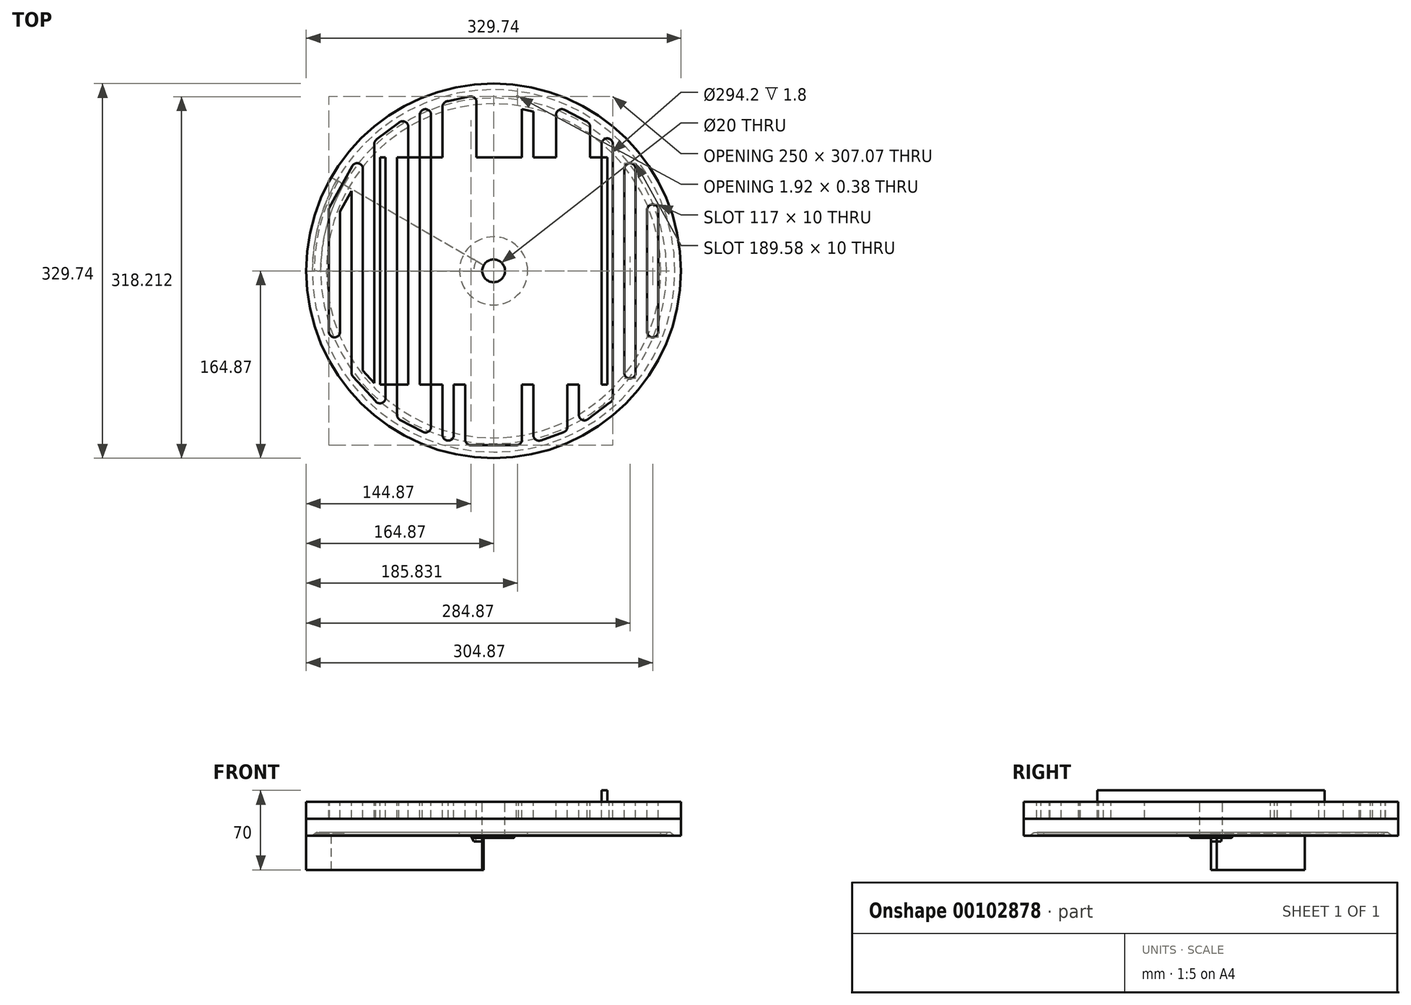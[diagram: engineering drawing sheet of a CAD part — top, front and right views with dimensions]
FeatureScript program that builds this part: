
annotation { "Feature Type Name" : "Feature", "Feature Type Description" : "" }
export const myFeature = defineFeature(function(context is Context, id is Id, definition is map)
    precondition{}
    {
        {
            var Q0;
            Q0=qCreatedBy(makeId("Front.planeOp"),FACE);
            var sketch = newSketch(context, id + "F0", { "sketchPlane" : qUnion([Q0])});
            skLineSegment(sketch, "E0", {"start": v(-152.8, 6.54) * mm, "end": v(-147.1, 6.54) * mm});
            skLineSegment(sketch, "E1", {"start": v(0, 31.7) * mm, "end": v(0, -32.2) * mm});
            skLineSegment(sketch, "E2", {"start": v(-19.86, 6.26) * mm, "end": v(-17.5, 1.54) * mm});
            skLineSegment(sketch, "E3.0", {"start": v(-155.24, 8.34) * mm, "end": v(-153.54, 8.34) * mm});
            skLineSegment(sketch, "E4", {"start": v(-155.48, 8.26) * mm, "end": v(-157.85, 6.54) * mm});
            skPoint(sketch, "E5.visualSharp", {"position": v(-153.6, 6.54) * mm});
            skArc(sketch, "E5.filletArc", {"start": v(-153.1, 6.79) * mm, "mid": v(-153, 6.6) * mm, "end": v(-152.8, 6.54) * mm});
            skLineSegment(sketch, "E6", {"start": v(-153.34, 8.17) * mm, "end": v(-153.1, 6.79) * mm});
            skPoint(sketch, "E7.visualSharp", {"position": v(-153.37, 8.34) * mm});
            skArc(sketch, "E7.filletArc", {"start": v(-153.34, 8.17) * mm, "mid": v(-153.41, 8.3) * mm, "end": v(-153.54, 8.34) * mm});
            skPoint(sketch, "E8.visualSharp", {"position": v(-155.37, 8.34) * mm});
            skArc(sketch, "E8.filletArc", {"start": v(-155.24, 8.34) * mm, "mid": v(-155.37, 8.32) * mm, "end": v(-155.48, 8.26) * mm});
            skPoint(sketch, "E9.visualSharp", {"position": v(-20, 6.54) * mm});
            skArc(sketch, "E9.filletArc", {"start": v(-19.86, 6.26) * mm, "mid": v(-20.05, 6.46) * mm, "end": v(-20.3, 6.54) * mm});
            skLineSegment(sketch, "E10.0", {"start": v(-10, -3.46) * mm, "end": v(-10, -23.46) * mm});
            skPoint(sketch, "E11.endSnap0", {"position": v(-155.37, 8.32) * mm});
            skLineSegment(sketch, "E12.0", {"start": v(-164.87, 1.45) * mm, "end": v(-164.87, -23.46) * mm});
            skLineSegment(sketch, "E13.0", {"start": v(-164.87, -23.46) * mm, "end": v(-10, -23.46) * mm});
            skLineSegment(sketch, "E14.0", {"start": v(-147.1, 9.34) * mm, "end": v(-147.1, 7.54) * mm});
            skLineSegment(sketch, "E15", {"start": v(-154.4, 8.34) * mm, "end": v(-153.37, 8.34) * mm});
            skLineSegment(sketch, "E16", {"start": v(-10, -7.75) * mm, "end": v(-10, 8.34) * mm});
            skPoint(sketch, "E17.orphan", {"position": v(0, 8.34) * mm});
            skLineSegment(sketch, "E18", {"start": v(-164.87, 1.45) * mm, "end": v(-164.87, 36.54) * mm});
            skLineSegment(sketch, "E19", {"start": v(-164.87, 36.54) * mm, "end": v(-10, 36.54) * mm});
            skLineSegment(sketch, "E20", {"start": v(-10, 36.54) * mm, "end": v(-10, 8.34) * mm});
            skLineSegment(sketch, "E21", {"start": v(-30, 9.34) * mm, "end": v(-30, 7.54) * mm});
            skPoint(sketch, "E22.start.orphan", {"position": v(-15, -3.46) * mm});
            skLineSegment(sketch, "E23.trimOffspring", {"start": v(-30, 6.54) * mm, "end": v(-20.3, 6.54) * mm});
            skLineSegment(sketch, "E24", {"start": v(-17.5, 1.54) * mm, "end": v(-10, 1.54) * mm});
            skLineSegment(sketch, "E25", {"start": v(-164.87, 6.54) * mm, "end": v(-30, 6.54) * mm});
            skLineSegment(sketch, "E26.0", {"start": v(-17.25, 4.52) * mm, "end": v(-9.64, 4.52) * mm});
            skLineSegment(sketch, "E27.0", {"start": v(-152.22, 7.54) * mm, "end": v(-147.1, 7.54) * mm});
            skLineSegment(sketch, "E28.0", {"start": v(-156.06, 9.07) * mm, "end": v(-159.56, 6.54) * mm});
            skArc(sketch, "E29.0", {"start": v(-155.24, 9.34) * mm, "mid": v(-155.67, 9.27) * mm, "end": v(-156.06, 9.07) * mm});
            skLineSegment(sketch, "E30.0", {"start": v(-155.24, 9.34) * mm, "end": v(-153.04, 9.34) * mm});
            skLineSegment(sketch, "E31.0", {"start": v(-152.44, 8.84) * mm, "end": v(-152.22, 7.54) * mm});
            skLineSegment(sketch, "E32.0", {"start": v(-147.1, 9.34) * mm, "end": v(-30, 9.34) * mm});
            skLineSegment(sketch, "E33.0", {"start": v(-30, 7.54) * mm, "end": v(-20.3, 7.54) * mm});
            skLineSegment(sketch, "E34.0", {"start": v(-18.97, 6.7) * mm, "end": v(-18.15, 5.07) * mm});
            skArc(sketch, "E35.0", {"start": v(-18.97, 6.7) * mm, "mid": v(-19.52, 7.31) * mm, "end": v(-20.3, 7.54) * mm});
            skPoint(sketch, "E36.trimOffspring.end.orphan", {"position": v(-30, 8.34) * mm});
            skPoint(sketch, "E37.visualSharp", {"position": v(-152.53, 9.34) * mm});
            skArc(sketch, "E37.filletArc", {"start": v(-152.44, 8.84) * mm, "mid": v(-152.65, 9.2) * mm, "end": v(-153.04, 9.34) * mm});
            skPoint(sketch, "E38.visualSharp", {"position": v(-17.87, 4.52) * mm});
            skArc(sketch, "E38.filletArc", {"start": v(-18.15, 5.07) * mm, "mid": v(-17.78, 4.67) * mm, "end": v(-17.25, 4.52) * mm});
            skLineSegment(sketch, "E39", {"start": v(-147.1, 7.54) * mm, "end": v(-30, 7.54) * mm});
            skSolve(sketch);
        }
        {
            var Q0;
            {var subQ10=sQuery(id+"F0.wireOp",EDGE,"E9.filletArc");Q0=makeQuery(id+"F0.imprint","IMPRINT",FACE,{"disambiguationData":[TD([[makeQuery(id+"F0.imprint","IMPRINT",EDGE,{"derivedFrom":subQ10}),1.0]])]});}
            var Q1;
            {var subQ2=sQuery(id+"F0.wireOp",EDGE,"E3.0");Q1=makeQuery(id+"F0.imprint","IMPRINT",FACE,{"disambiguationData":[TD([[makeQuery(id+"F0.imprint","IMPRINT",EDGE,{"derivedFrom":subQ2}),-1.0]])]});}
            var Q2;
            Q2=sQuery(id+"F0.wireOp",EDGE,"E1");
            revolve(context, id + "F1", {"entities" : qUnion([Q0, Q1]), "axis" : qUnion([Q2]), "revolveType" : RevolveType.ONE_DIRECTION, "angle" : 30 * degree});
        }
        {
            var Q0;
            {var subQ2=sQuery(id+"F0.wireOp",EDGE,"E9.filletArc");Q0=makeQuery(id+"F0.imprint","IMPRINT",FACE,{"disambiguationData":[TD([[makeQuery(id+"F0.imprint","IMPRINT",EDGE,{"derivedFrom":subQ2}),-1.0]])]});}
            var Q1;
            {var subQ1=sQuery(id+"F0.wireOp",EDGE,"E3.0");Q1=makeQuery(id+"F0.imprint","IMPRINT",FACE,{"disambiguationData":[TD([[makeQuery(id+"F0.imprint","IMPRINT",EDGE,{"derivedFrom":subQ1}),1.0]])]});}
            var Q2;
            Q2=sQuery(id+"F0.wireOp",EDGE,"E1");
            revolve(context, id + "F2", {"entities" : qUnion([Q0, Q1]), "axis" : qUnion([Q2]), "revolveType" : RevolveType.ONE_DIRECTION, "angle" : 30 * degree});
        }
        {
            var Q0;
            Q0=makeQuery(id+"F2.opRevolve","SWEPT_BODY",BODY,{"disambiguationData":[OSD([sQuery(id+"F0.wireOp",EDGE,"E2"),sQuery(id+"F0.wireOp",EDGE,"E3.0"),sQuery(id+"F0.wireOp",EDGE,"E4"),sQuery(id+"F0.wireOp",EDGE,"E5.filletArc"),sQuery(id+"F0.wireOp",EDGE,"E6"),sQuery(id+"F0.wireOp",EDGE,"E7.filletArc"),sQuery(id+"F0.wireOp",EDGE,"E8.filletArc"),sQuery(id+"F0.wireOp",EDGE,"E9.filletArc"),sQuery(id+"F0.wireOp",EDGE,"E14.0"),sQuery(id+"F0.wireOp",EDGE,"E15"),sQuery(id+"F0.wireOp",EDGE,"E16"),sQuery(id+"F0.wireOp",EDGE,"E18"),sQuery(id+"F0.wireOp",EDGE,"E19"),sQuery(id+"F0.wireOp",EDGE,"E20"),sQuery(id+"F0.wireOp",EDGE,"E36.trimOffspring"),sQuery(id+"F0.wireOp",EDGE,"E21"),sQuery(id+"F0.wireOp",EDGE,"E23.trimOffspring"),sQuery(id+"F0.wireOp",EDGE,"E25"),sQuery(id+"F0.wireOp",EDGE,"E26.0")])]});
            transform(context, id + "F3", {"entities" : qUnion([Q0]), "transformType" : TransformType.TRANSLATION_3D, "dx" : 0 * mm, "dy" : 0 * mm, "dz" : 0 * mm, "makeCopy" : false});
        }
        {
            var Q0;
            Q0=makeQuery(id+"F0.imprint","IMPRINT",FACE,{"disambiguationData":[TD([[makeQuery(id+"F0.imprint","IMPRINT",EDGE,{"derivedFrom":sQuery(id+"F0.wireOp",EDGE,"E14.0")}),-1.0]])]});
            var Q1;
            Q1=sQuery(id+"F0.wireOp",EDGE,"E1");
            revolve(context, id + "F4", {"entities" : qUnion([Q0]), "axis" : qUnion([Q1]), "revolveType" : RevolveType.FULL});
        }
        {
            var Q0;
            Q0=makeQuery(id+"F4.opRevolve","SWEPT_BODY",BODY,{"disambiguationData":[OSD([sQuery(id+"F0.wireOp",EDGE,"E14.0"),sQuery(id+"F0.wireOp",EDGE,"E16"),sQuery(id+"F0.wireOp",EDGE,"E18"),sQuery(id+"F0.wireOp",EDGE,"E19"),sQuery(id+"F0.wireOp",EDGE,"E20"),sQuery(id+"F0.wireOp",EDGE,"E21"),sQuery(id+"F0.wireOp",EDGE,"E25"),sQuery(id+"F0.wireOp",EDGE,"E26.0"),sQuery(id+"F0.wireOp",EDGE,"E27.0"),sQuery(id+"F0.wireOp",EDGE,"E28.0"),sQuery(id+"F0.wireOp",EDGE,"E29.0"),sQuery(id+"F0.wireOp",EDGE,"E30.0"),sQuery(id+"F0.wireOp",EDGE,"E31.0"),sQuery(id+"F0.wireOp",EDGE,"E32.0"),sQuery(id+"F0.wireOp",EDGE,"E33.0"),sQuery(id+"F0.wireOp",EDGE,"E34.0"),sQuery(id+"F0.wireOp",EDGE,"E35.0"),sQuery(id+"F0.wireOp",EDGE,"E37.filletArc"),sQuery(id+"F0.wireOp",EDGE,"E38.filletArc")])]});
            transform(context, id + "F5", {"entities" : qUnion([Q0]), "transformType" : TransformType.TRANSLATION_3D, "dx" : 0 * mm, "dy" : 0 * mm, "dz" : 0 * mm, "makeCopy" : false});
        }
        {
            var Q0;
            Q0=makeQuery(id+"F4.opRevolve","SWEPT_FACE",FACE,{"disambiguationData":[OSD([sQuery(id+"F0.wireOp",EDGE,"E19")])]});
            var sketch = newSketch(context, id + "F6", { "sketchPlane" : qUnion([Q0])});
            skLineSegment(sketch, "E40.right", {"start": v(100, 100) * mm, "end": v(100, -100) * mm});
            skPoint(sketch, "E40.middle", {"position": v(0, 0) * mm});
            skLineSegment(sketch, "E41.4.0.0", {"start": v(100, 111.64) * mm, "end": v(100, -111.64) * mm});
            skLineSegment(sketch, "E41.5.0.0", {"start": v(120, 89.8) * mm, "end": v(120, -89.8) * mm});
            skLineSegment(sketch, "E41.6.0.0", {"start": v(140, 53.5) * mm, "end": v(140, -53.5) * mm});
            skLineSegment(sketch, "E41.direction1", {"start": v(20, -149.87) * mm, "end": v(40, -149.87) * mm, "construction": true});
            skLineSegment(sketch, "E42.direction1", {"start": v(-20, -149.87) * mm, "end": v(-40, -149.87) * mm, "construction": true});
            skArc(sketch, "E43.0.startCap", {"start": v(-124.38, 92.2) * mm, "mid": v(-118.75, 94.63) * mm, "end": v(-115, 89.8) * mm});
            skArc(sketch, "E43.0.endCap", {"start": v(-123.69, -93.17) * mm, "mid": v(-124.66, -91.6) * mm, "end": v(-125, -89.8) * mm});
            skLineSegment(sketch, "E43.0.left", {"start": v(-115, 89.8) * mm, "end": v(-115, -87.85) * mm});
            skLineSegment(sketch, "E43.0.right", {"start": v(-125, 70.36) * mm, "end": v(-125, -89.8) * mm});
            skArc(sketch, "E43.1.startCap", {"start": v(-145, 53.5) * mm, "mid": v(-144.83, 54.79) * mm, "end": v(-144.34, 55.99) * mm});
            skArc(sketch, "E43.1.endCap", {"start": v(-135, -53.5) * mm, "mid": v(-140, -58.5) * mm, "end": v(-145, -53.5) * mm});
            skLineSegment(sketch, "E43.1.left", {"start": v(-135, 52.21) * mm, "end": v(-135, -53.5) * mm});
            skLineSegment(sketch, "E43.1.right", {"start": v(-145, 53.5) * mm, "end": v(-145, -53.5) * mm});
            skArc(sketch, "E43.2.startCap", {"start": v(-105, 111.64) * mm, "mid": v(-104.48, 113.87) * mm, "end": v(-103.01, 115.63) * mm});
            skArc(sketch, "E43.2.endCap", {"start": v(-95, -111.64) * mm, "mid": v(-98.28, -116.33) * mm, "end": v(-103.82, -114.86) * mm});
            skLineSegment(sketch, "E43.2.left", {"start": v(-95, 109.14) * mm, "end": v(-95, -111.64) * mm});
            skLineSegment(sketch, "E43.2.right", {"start": v(-105, 111.64) * mm, "end": v(-105, -98.77) * mm});
            skArc(sketch, "E43.3.startCap", {"start": v(-83.28, 130.51) * mm, "mid": v(-77.93, 131.29) * mm, "end": v(-75, 126.74) * mm});
            skArc(sketch, "E43.3.endCap", {"start": v(-82.34, -131.16) * mm, "mid": v(-84.28, -129.32) * mm, "end": v(-85, -126.74) * mm});
            skLineSegment(sketch, "E43.3.left", {"start": v(-75, 126.74) * mm, "end": v(-75, -123.73) * mm});
            skLineSegment(sketch, "E43.3.right", {"start": v(-85, 116.69) * mm, "end": v(-85, -126.74) * mm});
            skArc(sketch, "E43.4.startCap", {"start": v(-65, 137.34) * mm, "mid": v(-60, 142.34) * mm, "end": v(-55, 137.34) * mm});
            skArc(sketch, "E43.4.endCap", {"start": v(-55, -137.34) * mm, "mid": v(-57.64, -141.75) * mm, "end": v(-62.77, -141.5) * mm});
            skLineSegment(sketch, "E43.4.left", {"start": v(-55, 137.34) * mm, "end": v(-55, -137.34) * mm});
            skLineSegment(sketch, "E43.4.right", {"start": v(-65, 137.34) * mm, "end": v(-65, -129.01) * mm});
            skArc(sketch, "E43.5.startCap", {"start": v(-45, 144.44) * mm, "mid": v(-43.54, 147.97) * mm, "end": v(-40, 149.44) * mm});
            skArc(sketch, "E43.5.endCap", {"start": v(-35, -144.44) * mm, "mid": v(-40, -149.44) * mm, "end": v(-45, -144.44) * mm});
            skLineSegment(sketch, "E43.5.left", {"start": v(-35, 140.27) * mm, "end": v(-35, -144.44) * mm});
            skLineSegment(sketch, "E43.5.right", {"start": v(-45, 144.44) * mm, "end": v(-45, -144.44) * mm});
            skArc(sketch, "E43.6.startCap", {"start": v(-21.03, 153.43) * mm, "mid": v(-16.85, 152.42) * mm, "end": v(-15, 148.53) * mm});
            skArc(sketch, "E43.6.endCap", {"start": v(-20, -153.53) * mm, "mid": v(-23.54, -152.07) * mm, "end": v(-25, -148.53) * mm});
            skLineSegment(sketch, "E43.6.left", {"start": v(-15, 148.53) * mm, "end": v(-15, -143.53) * mm});
            skLineSegment(sketch, "E43.6.right", {"start": v(-25, 142.37) * mm, "end": v(-25, -148.53) * mm});
            skArc(sketch, "E43.8.startCap", {"start": v(15, 148.53) * mm, "mid": v(17.23, 152.7) * mm, "end": v(21.92, 153.15) * mm});
            skArc(sketch, "E43.8.endCap", {"start": v(25, -148.53) * mm, "mid": v(23.54, -152.07) * mm, "end": v(20, -153.53) * mm});
            skLineSegment(sketch, "E43.8.left", {"start": v(25, 142.34) * mm, "end": v(25, -148.53) * mm});
            skLineSegment(sketch, "E43.8.right", {"start": v(15, 148.53) * mm, "end": v(15, -143.53) * mm});
            skArc(sketch, "E43.9.startCap", {"start": v(40, 149.44) * mm, "mid": v(43.54, 147.97) * mm, "end": v(45, 144.44) * mm});
            skLineSegment(sketch, "E43.9.left", {"start": v(45, 144.44) * mm, "end": v(45, -137.44) * mm});
            skLineSegment(sketch, "E43.9.right", {"start": v(35, 140.34) * mm, "end": v(35, -144.56) * mm});
            skArc(sketch, "E43.10.startCap", {"start": v(55, 137.34) * mm, "mid": v(60, 142.34) * mm, "end": v(65, 137.34) * mm});
            skArc(sketch, "E43.10.endCap", {"start": v(65, -137.34) * mm, "mid": v(64.1, -140.21) * mm, "end": v(61.7, -142.04) * mm});
            skLineSegment(sketch, "E43.10.left", {"start": v(65, 137.34) * mm, "end": v(65, -137.34) * mm});
            skLineSegment(sketch, "E43.10.right", {"start": v(55, 137.34) * mm, "end": v(55, -133.83) * mm});
            skArc(sketch, "E43.11.startCap", {"start": v(75, 126.74) * mm, "mid": v(80, 131.74) * mm, "end": v(85, 126.74) * mm});
            skArc(sketch, "E43.11.endCap", {"start": v(83.04, -130.7) * mm, "mid": v(77.79, -131.22) * mm, "end": v(75, -126.74) * mm});
            skLineSegment(sketch, "E43.11.left", {"start": v(85, 126.74) * mm, "end": v(85, -116.6) * mm});
            skLineSegment(sketch, "E43.11.right", {"start": v(75, 126.74) * mm, "end": v(75, -126.74) * mm});
            skArc(sketch, "E43.12.startCap", {"start": v(95, 111.64) * mm, "mid": v(100, 116.64) * mm, "end": v(105, 111.64) * mm});
            skArc(sketch, "E43.12.endCap", {"start": v(105, -111.64) * mm, "mid": v(104.13, -114.46) * mm, "end": v(101.81, -116.3) * mm});
            skLineSegment(sketch, "E43.12.left", {"start": v(105, 111.64) * mm, "end": v(105, -111.64) * mm});
            skLineSegment(sketch, "E43.12.right", {"start": v(95, 111.64) * mm, "end": v(95, -108.92) * mm});
            skArc(sketch, "E43.13.startCap", {"start": v(115, 89.8) * mm, "mid": v(120, 94.8) * mm, "end": v(125, 89.8) * mm});
            skArc(sketch, "E43.13.endCap", {"start": v(125, -89.8) * mm, "mid": v(120, -94.8) * mm, "end": v(115, -89.8) * mm});
            skLineSegment(sketch, "E43.13.left", {"start": v(125, 89.8) * mm, "end": v(125, -89.8) * mm});
            skLineSegment(sketch, "E43.13.right", {"start": v(115, 89.8) * mm, "end": v(115, -89.8) * mm});
            skArc(sketch, "E43.14.startCap", {"start": v(135, 53.5) * mm, "mid": v(140, 58.5) * mm, "end": v(145, 53.5) * mm});
            skArc(sketch, "E43.14.endCap", {"start": v(145, -53.5) * mm, "mid": v(140, -58.5) * mm, "end": v(135, -53.5) * mm});
            skLineSegment(sketch, "E43.14.left", {"start": v(145, 53.5) * mm, "end": v(145, -53.5) * mm});
            skLineSegment(sketch, "E43.14.right", {"start": v(135, 53.5) * mm, "end": v(135, -53.5) * mm});
            skLineSegment(sketch, "E44.bottom", {"start": v(100, 100) * mm, "end": v(-100, 100) * mm});
            skLineSegment(sketch, "E44.top", {"start": v(100, -100) * mm, "end": v(-100, -100) * mm});
            skLineSegment(sketch, "E44.right", {"start": v(-100, 100) * mm, "end": v(-100, -100) * mm});
            skLineSegment(sketch, "E45", {"start": v(-83.28, 130.51) * mm, "end": v(-103.01, 115.63) * mm});
            skLineSegment(sketch, "E46.0", {"start": v(-85, 116.69) * mm, "end": v(-95, 109.14) * mm});
            skLineSegment(sketch, "E47", {"start": v(-144.34, 55.99) * mm, "end": v(-124.38, 92.2) * mm});
            skLineSegment(sketch, "E48.0", {"start": v(-135, 52.21) * mm, "end": v(-125, 70.36) * mm});
            skLineSegment(sketch, "E49", {"start": v(-103.82, -114.86) * mm, "end": v(-123.69, -93.17) * mm});
            skLineSegment(sketch, "E50.0", {"start": v(-105, -98.77) * mm, "end": v(-115, -87.85) * mm});
            skLineSegment(sketch, "E51", {"start": v(-62.77, -141.5) * mm, "end": v(-82.34, -131.16) * mm});
            skLineSegment(sketch, "E52.0", {"start": v(-65, -129.01) * mm, "end": v(-75, -123.73) * mm});
            skLineSegment(sketch, "E53.trimOffspring", {"start": v(-100, -100) * mm, "end": v(-100, -104.23) * mm});
            skLineSegment(sketch, "E54", {"start": v(-40, 149.44) * mm, "end": v(-21.03, 153.43) * mm});
            skLineSegment(sketch, "E55.0", {"start": v(-35, 140.27) * mm, "end": v(-25, 142.37) * mm});
            skLineSegment(sketch, "E56", {"start": v(-20, -153.53) * mm, "end": v(20, -153.53) * mm});
            skLineSegment(sketch, "E57.0", {"start": v(-15, -143.53) * mm, "end": v(15, -143.53) * mm});
            skLineSegment(sketch, "E58", {"start": v(20, 153.53) * mm, "end": v(40, 149.54) * mm});
            skPoint(sketch, "E58.endSnap0", {"position": v(40, 149.44) * mm});
            skLineSegment(sketch, "E59.0", {"start": v(25, 142.34) * mm, "end": v(35, 140.34) * mm});
            skLineSegment(sketch, "E60", {"start": v(41.7, -149.26) * mm, "end": v(61.7, -142.04) * mm});
            skPoint(sketch, "E60.endSnap0", {"position": v(60, -142.34) * mm});
            skLineSegment(sketch, "E61.0", {"start": v(45, -137.44) * mm, "end": v(55, -133.83) * mm});
            skPoint(sketch, "E62.orphan", {"position": v(60.87, -142.34) * mm});
            skArc(sketch, "E63.filletArc", {"start": v(35, -144.56) * mm, "mid": v(37.13, -148.65) * mm, "end": v(41.7, -149.26) * mm});
            skLineSegment(sketch, "E64", {"start": v(82.24, 131.2) * mm, "end": v(62.34, 141.76) * mm});
            skLineSegment(sketch, "E65.0", {"start": v(77.55, 122.37) * mm, "end": v(57.66, 132.92) * mm});
            skLineSegment(sketch, "E66", {"start": v(101.81, -116.3) * mm, "end": v(83.04, -130.7) * mm});
            skLineSegment(sketch, "E67.0", {"start": v(95.73, -108.36) * mm, "end": v(85, -116.6) * mm});
            skSolve(sketch);
        }
        {
            var Q0;
            Q0=makeQuery(id+"F6.imprint","IMPRINT",FACE,{"disambiguationData":[TD([[makeQuery(id+"F6.imprint","IMPRINT",EDGE,{"derivedFrom":sQuery(id+"F6.wireOp",EDGE,"E40.right")}),-1.0]])]});
            var Q1;
            Q1=makeQuery(id+"F6.imprint","IMPRINT",FACE,{"disambiguationData":[TD([[makeQuery(id+"F6.imprint","IMPRINT",EDGE,{"derivedFrom":sQuery(id+"F6.wireOp",EDGE,"E40.left")}),1.0]])]});
            extrude(context, id + "F7", {"entities" : qUnion([Q0, Q1]), "operationType" : NewBodyOperationType.ADD, "depth" : 10 * mm});
        }
        {
            var Q0;
            Q0=makeQuery(id+"F6.imprint","IMPRINT",FACE,{"disambiguationData":[TD([[makeQuery(id+"F6.imprint","IMPRINT",EDGE,{"derivedFrom":sQuery(id+"F6.wireOp",EDGE,"E43.0.startCap")}),-1.0]])]});
            var Q1;
            {var subQ5=sQuery(id+"F6.wireOp",EDGE,"E44.right");Q1=makeQuery(id+"F6.imprint","IMPRINT",FACE,{"disambiguationData":[TD([[makeQuery(id+"F6.imprint","IMPRINT",EDGE,{"derivedFrom":subQ5}),1.0]])]});}
            var Q2;
            {var subQ0=sQuery(id+"F6.wireOp",EDGE,"E44.bottom");var subQ1=sQuery(id+"F6.wireOp",EDGE,"E43.3.left");var subQ2=makeQuery(id+"F6.imprint","INTERSECT",VERTEX,{"derivedFrom":[subQ1,subQ0]});Q2=makeQuery(id+"F6.imprint","IMPRINT",FACE,{"disambiguationData":[TD([[makeQuery(id+"F6.imprint","IMPRINT",EDGE,{"disambiguationData":[TD([[subQ2,-1.0]])],"derivedFrom":subQ1}),-1.0]])]});}
            var Q3;
            {var subQ1=sQuery(id+"F6.wireOp",EDGE,"E43.3.endCap");Q3=makeQuery(id+"F6.imprint","IMPRINT",FACE,{"disambiguationData":[TD([[makeQuery(id+"F6.imprint","IMPRINT",EDGE,{"derivedFrom":subQ1}),-1.0]])]});}
            var Q4;
            {var subQ0=sQuery(id+"F6.wireOp",EDGE,"E44.bottom");var subQ1=sQuery(id+"F6.wireOp",EDGE,"E43.4.left");var subQ2=makeQuery(id+"F6.imprint","INTERSECT",VERTEX,{"derivedFrom":[subQ1,subQ0]});Q4=makeQuery(id+"F6.imprint","IMPRINT",FACE,{"disambiguationData":[TD([[makeQuery(id+"F6.imprint","IMPRINT",EDGE,{"disambiguationData":[TD([[subQ2,-1.0]])],"derivedFrom":subQ1}),-1.0]])]});}
            var Q5;
            {var subQ0=sQuery(id+"F6.wireOp",EDGE,"E43.4.startCap");Q5=makeQuery(id+"F6.imprint","IMPRINT",FACE,{"disambiguationData":[TD([[makeQuery(id+"F6.imprint","IMPRINT",EDGE,{"derivedFrom":subQ0}),-1.0]])]});}
            extrude(context, id + "F8", {"entities" : qUnion([Q0, Q1, Q2, Q3, Q4, Q5]), "oppositeDirection" : true, "depth" : 15 * mm});
        }
    });
